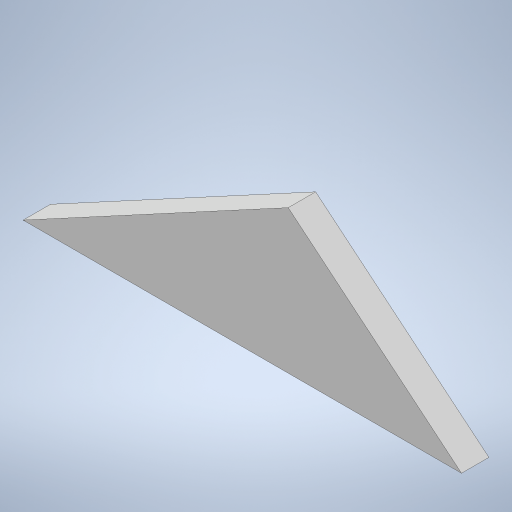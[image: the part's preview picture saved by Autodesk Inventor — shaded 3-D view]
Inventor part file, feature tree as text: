
AUTODESK INVENTOR PART (.ipt)
format: ipt  version: 2023 (Build 270158000, 158)  size: 210,944 bytes
history: native  units: mm
features: other x1, extrude x1, sketch x1
ambient origin geometry x8: Origin, YZ Plane, XZ Plane, XY Plane, X Axis, Y Axis, Z Axis, Center Point
bodies: Body1 (feature_tree)
feature tree (3):
  other  "Bryła1"
  extrude  "Wyciągnięcie proste1"  Depth=80.0mm
  sketch  "Szkic1"
